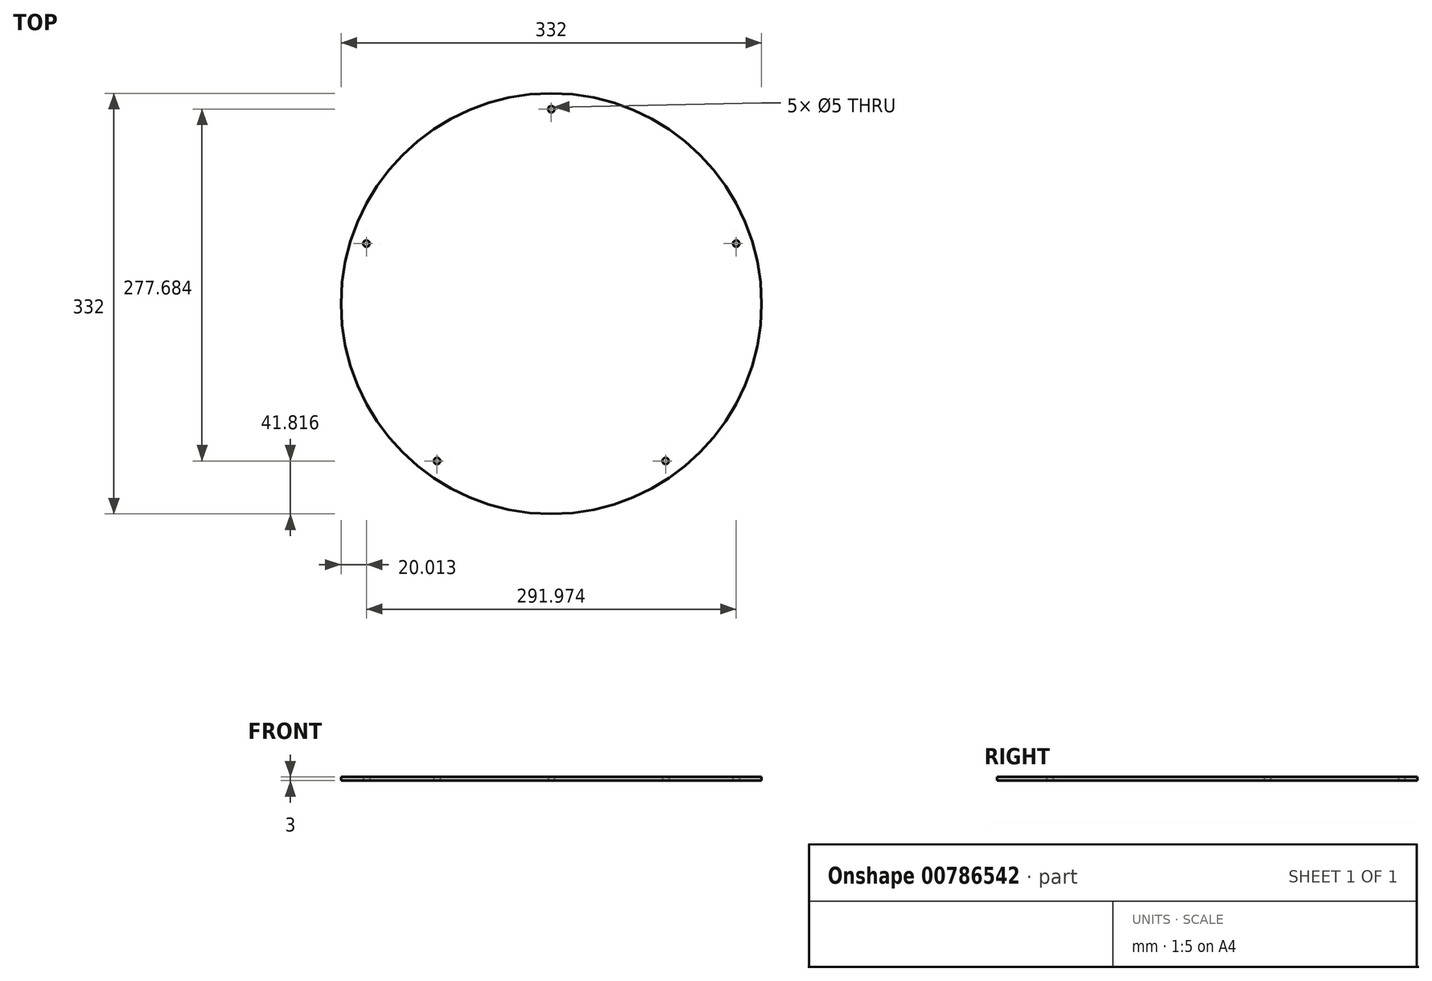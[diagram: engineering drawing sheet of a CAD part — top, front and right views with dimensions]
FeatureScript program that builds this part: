
annotation { "Feature Type Name" : "Feature", "Feature Type Description" : "" }
export const myFeature = defineFeature(function(context is Context, id is Id, definition is map)
    precondition{}
    {
        {
            var Q0;
            Q0=qCreatedBy(makeId("Top.planeOp"),FACE);
            var sketch = newSketch(context, id + "F0", { "sketchPlane" : qUnion([Q0])});
            skCircle(sketch, "E0", {"center": v(0, 0) * mm, "radius": 166 * mm});
            skLineSegment(sketch, "E1", {"start": v(0, 0) * mm, "end": v(0, 166) * mm});
            skCircle(sketch, "E2", {"center": v(0, 153.5) * mm, "radius": 2.5 * mm});
            skPoint(sketch, "E3", {"position": v(0, 156) * mm});
            skLineSegment(sketch, "E4", {"start": v(0, 0) * mm, "end": v(157.88, 51.3) * mm});
            skLineSegment(sketch, "E5", {"start": v(0, 0) * mm, "end": v(97.57, -134.3) * mm});
            skLineSegment(sketch, "E6", {"start": v(0, 0) * mm, "end": v(-97.57, -134.3) * mm});
            skLineSegment(sketch, "E7", {"start": v(0, 0) * mm, "end": v(-157.88, 51.3) * mm});
            skCircle(sketch, "E8.1.0", {"center": v(-145.99, 47.43) * mm, "radius": 2.5 * mm});
            skCircle(sketch, "E8.2.0", {"center": v(-90.23, -124.18) * mm, "radius": 2.5 * mm});
            skCircle(sketch, "E8.3.0", {"center": v(90.23, -124.18) * mm, "radius": 2.5 * mm});
            skCircle(sketch, "E8.4.0", {"center": v(145.99, 47.43) * mm, "radius": 2.5 * mm});
            skSolve(sketch);
        }
        {
            var Q0;
            {var subQ1=sQuery(id+"F0.wireOp",EDGE,"E1");var subQ4=sQuery(id+"F0.wireOp",EDGE,"E0");var subQ5=makeQuery(id+"F0.imprint","INTERSECT",VERTEX,{"derivedFrom":[subQ4,subQ1]});Q0=makeQuery(id+"F0.imprint","IMPRINT",FACE,{"disambiguationData":[TD([[makeQuery(id+"F0.imprint","IMPRINT",EDGE,{"disambiguationData":[TD([[subQ5,1.0]])],"derivedFrom":subQ4}),1.0]])]});}
            var Q1;
            {var subQ1=sQuery(id+"F0.wireOp",EDGE,"E4");var subQ5=sQuery(id+"F0.wireOp",EDGE,"E0");var subQ6=makeQuery(id+"F0.imprint","INTERSECT",VERTEX,{"derivedFrom":[subQ5,subQ1]});Q1=makeQuery(id+"F0.imprint","IMPRINT",FACE,{"disambiguationData":[TD([[makeQuery(id+"F0.imprint","IMPRINT",EDGE,{"disambiguationData":[TD([[subQ6,1.0]])],"derivedFrom":subQ5}),1.0]])]});}
            var Q2;
            {var subQ1=sQuery(id+"F0.wireOp",EDGE,"E5");var subQ8=sQuery(id+"F0.wireOp",EDGE,"E0");var subQ9=makeQuery(id+"F0.imprint","INTERSECT",VERTEX,{"derivedFrom":[subQ8,subQ1]});Q2=makeQuery(id+"F0.imprint","IMPRINT",FACE,{"disambiguationData":[TD([[makeQuery(id+"F0.imprint","IMPRINT",EDGE,{"disambiguationData":[TD([[subQ9,1.0]])],"derivedFrom":subQ8}),1.0]])]});}
            var Q3;
            {var subQ1=sQuery(id+"F0.wireOp",EDGE,"E6");var subQ5=sQuery(id+"F0.wireOp",EDGE,"E0");var subQ6=makeQuery(id+"F0.imprint","INTERSECT",VERTEX,{"derivedFrom":[subQ5,subQ1]});Q3=makeQuery(id+"F0.imprint","IMPRINT",FACE,{"disambiguationData":[TD([[makeQuery(id+"F0.imprint","IMPRINT",EDGE,{"disambiguationData":[TD([[subQ6,1.0]])],"derivedFrom":subQ5}),1.0]])]});}
            var Q4;
            {var subQ1=sQuery(id+"F0.wireOp",EDGE,"E1");var subQ8=sQuery(id+"F0.wireOp",EDGE,"E0");var subQ9=makeQuery(id+"F0.imprint","INTERSECT",VERTEX,{"derivedFrom":[subQ8,subQ1]});Q4=makeQuery(id+"F0.imprint","IMPRINT",FACE,{"disambiguationData":[TD([[makeQuery(id+"F0.imprint","IMPRINT",EDGE,{"disambiguationData":[TD([[subQ9,-1.0]])],"derivedFrom":subQ8}),1.0]])]});}
            extrude(context, id + "F1", {"entities" : qUnion([Q0, Q1, Q2, Q3, Q4]), "depth" : 3 * mm, "offsetDistance" : 25 * mm});
        }
    });
